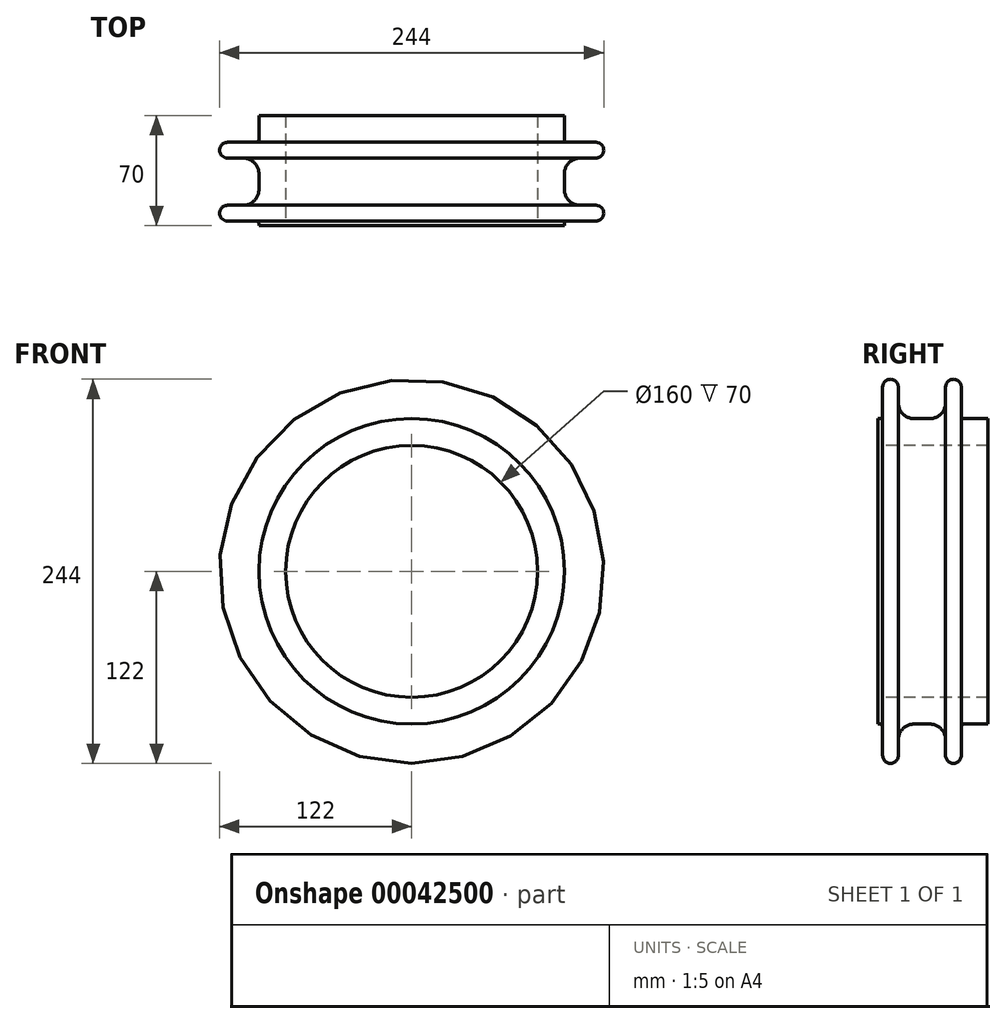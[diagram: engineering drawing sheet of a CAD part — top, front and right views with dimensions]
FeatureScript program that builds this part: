
annotation { "Feature Type Name" : "Feature", "Feature Type Description" : "" }
export const myFeature = defineFeature(function(context is Context, id is Id, definition is map)
    precondition{}
    {
        {
            var Q0;
            Q0=qCreatedBy(makeId("Right.planeOp"),FACE);
            var sketch = newSketch(context, id + "F0", { "sketchPlane" : qUnion([Q0])});
            skLineSegment(sketch, "E0", {"start": v(0, 97) * mm, "end": v(-5, 97) * mm});
            skArc(sketch, "E1", {"start": v(-15, 107) * mm, "mid": v(-12.07, 99.93) * mm, "end": v(-5, 97) * mm});
            skLineSegment(sketch, "E2", {"start": v(-15, 107) * mm, "end": v(-15, 117) * mm});
            skArc(sketch, "E3", {"start": v(-15, 117) * mm, "mid": v(-20, 122) * mm, "end": v(-25, 117) * mm});
            skLineSegment(sketch, "E4", {"start": v(-25, 117) * mm, "end": v(-25, 99) * mm});
            skArc(sketch, "E5", {"start": v(-27, 97) * mm, "mid": v(-25.59, 97.59) * mm, "end": v(-25, 99) * mm});
            skLineSegment(sketch, "E6", {"start": v(-27, 97) * mm, "end": v(-28, 97) * mm});
            skLineSegment(sketch, "E7", {"start": v(-28, 97) * mm, "end": v(-28, 80) * mm});
            skLineSegment(sketch, "E8", {"start": v(-26.05, 0) * mm, "end": v(0, 0) * mm, "construction": true});
            skLineSegment(sketch, "E9.MirrorCS", {"start": v(0, 97) * mm, "end": v(5, 97) * mm});
            skArc(sketch, "E10.MirrorCS", {"start": v(15, 107) * mm, "mid": v(12.07, 99.93) * mm, "end": v(5, 97) * mm});
            skLineSegment(sketch, "E11.MirrorCS", {"start": v(15, 107) * mm, "end": v(15, 117) * mm});
            skLineSegment(sketch, "E12.MirrorCS", {"start": v(25, 117) * mm, "end": v(25, 99) * mm});
            skLineSegment(sketch, "E13.MirrorCS", {"start": v(27, 97) * mm, "end": v(42, 97) * mm});
            skArc(sketch, "E14.MirrorCS", {"start": v(15, 117) * mm, "mid": v(20, 122) * mm, "end": v(25, 117) * mm});
            skArc(sketch, "E15.MirrorCS", {"start": v(27, 97) * mm, "mid": v(25.59, 97.59) * mm, "end": v(25, 99) * mm});
            skLineSegment(sketch, "E16", {"start": v(42, 97) * mm, "end": v(42, 80) * mm});
            skLineSegment(sketch, "E17", {"start": v(42, 0) * mm, "end": v(0, 0) * mm, "construction": true});
            skLineSegment(sketch, "E18", {"start": v(-28, 80) * mm, "end": v(42, 80) * mm});
            skSolve(sketch);
        }
        {
            var Q0;
            Q0=makeQuery(id+"F0.imprint","IMPRINT",FACE,{"disambiguationData":[TD([[makeQuery(id+"F0.imprint","IMPRINT",EDGE,{"derivedFrom":sQuery(id+"F0.wireOp",EDGE,"E0")}),1.0]])]});
            var Q1;
            Q1=sQuery(id+"F0.wireOp",EDGE,"E8");
            revolve(context, id + "F1", {"entities" : qUnion([Q0]), "axis" : qUnion([Q1]), "revolveType" : RevolveType.FULL});
        }
    });
